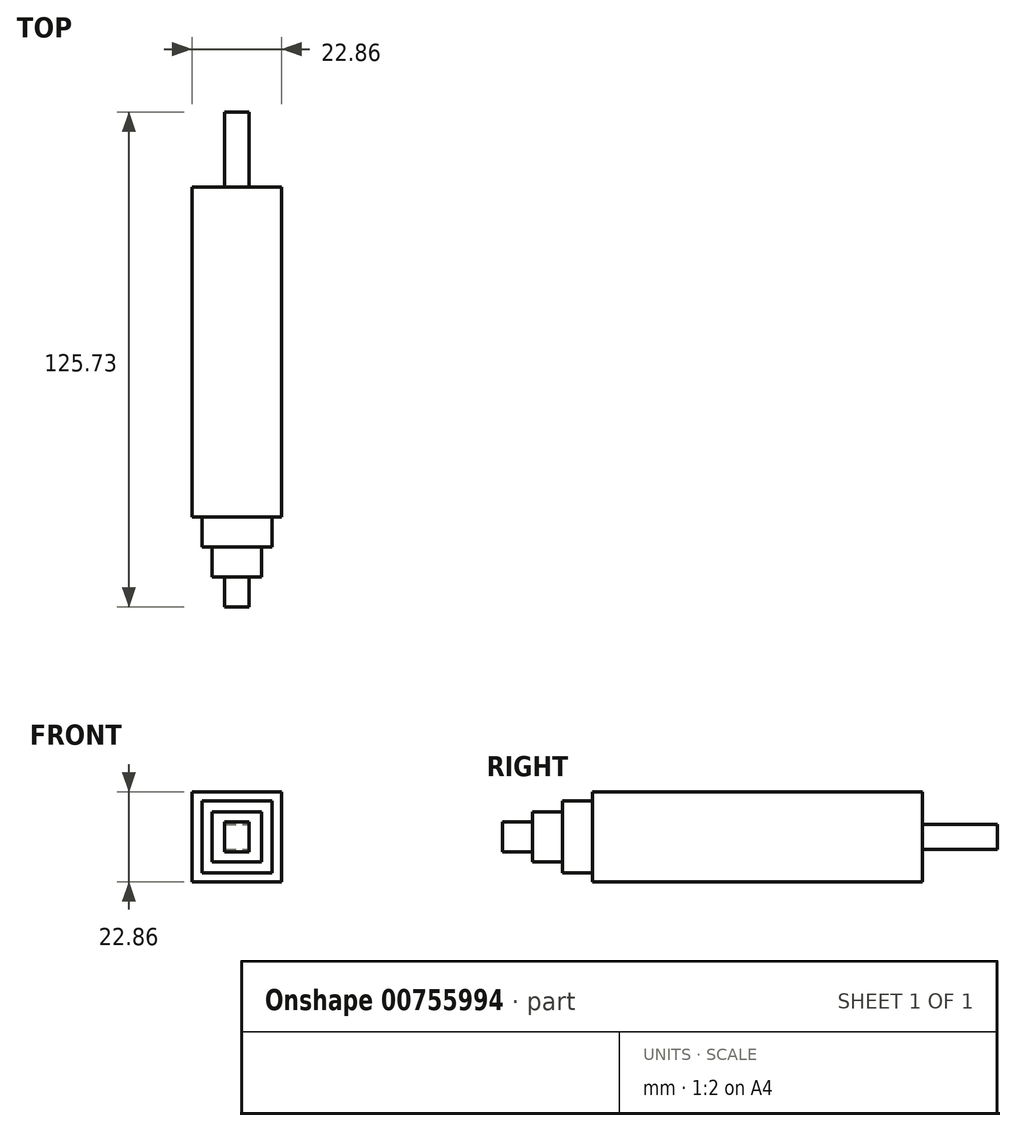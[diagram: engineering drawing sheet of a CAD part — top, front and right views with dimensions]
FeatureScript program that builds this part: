
annotation { "Feature Type Name" : "Feature", "Feature Type Description" : "" }
export const myFeature = defineFeature(function(context is Context, id is Id, definition is map)
    precondition{}
    {
        {
            var Q0;
            Q0=qCreatedBy(makeId("Top.planeOp"),FACE);
            var sketch = newSketch(context, id + "F0", { "sketchPlane" : qUnion([Q0])});
            skLineSegment(sketch, "E0.bottom", {"start": v(0, 0) * mm, "end": v(22.86, 0) * mm});
            skLineSegment(sketch, "E0.top", {"start": v(0, 83.82) * mm, "end": v(22.86, 83.82) * mm});
            skLineSegment(sketch, "E0.left", {"start": v(0, 0) * mm, "end": v(0, 83.82) * mm});
            skLineSegment(sketch, "E0.right", {"start": v(22.86, 0) * mm, "end": v(22.86, 83.82) * mm});
            skSolve(sketch);
        }
        {
            var Q0;
            Q0 = qSketchRegion(id + "F0", true);
            extrude(context, id + "F1", {"entities" : qUnion([Q0]), "depth" : 22.86 * mm, "offsetDistance" : 25.4 * mm});
        }
        {
            var Q0;
            Q0=makeQuery(id+"F1.opExtrude","SWEPT_FACE",FACE,{"disambiguationData":[OSD([sQuery(id+"F0.wireOp",EDGE,"E0.top")])]});
            var sketch = newSketch(context, id + "F2", { "sketchPlane" : qUnion([Q0])});
            skLineSegment(sketch, "E1", {"start": v(-22.86, 11.43) * mm, "end": v(-11.43, 11.43) * mm});
            skLineSegment(sketch, "E2.bottom", {"start": v(-8.25, 14.6) * mm, "end": v(-14.6, 14.6) * mm});
            skLineSegment(sketch, "E2.top", {"start": v(-8.25, 8.26) * mm, "end": v(-14.6, 8.26) * mm});
            skLineSegment(sketch, "E2.left", {"start": v(-8.25, 14.6) * mm, "end": v(-8.25, 8.26) * mm});
            skLineSegment(sketch, "E2.right", {"start": v(-14.6, 14.6) * mm, "end": v(-14.6, 8.26) * mm});
            skPoint(sketch, "E2.middle", {"position": v(-11.43, 11.43) * mm});
            skSolve(sketch);
        }
        {
            var Q0;
            Q0 = qSketchRegion(id + "F2", true);
            extrude(context, id + "F3", {"entities" : qUnion([Q0]), "operationType" : NewBodyOperationType.ADD, "depth" : 19.05 * mm, "offsetDistance" : 25.4 * mm});
        }
        {
            var Q0;
            Q0=makeQuery(id+"F1.opExtrude","SWEPT_FACE",FACE,{"disambiguationData":[OSD([sQuery(id+"F0.wireOp",EDGE,"E0.bottom")])]});
            var sketch = newSketch(context, id + "F4", { "sketchPlane" : qUnion([Q0])});
            skLineSegment(sketch, "E3", {"start": v(0, 11.43) * mm, "end": v(11.43, 11.43) * mm});
            skLineSegment(sketch, "E4.bottom", {"start": v(2.54, 20.56) * mm, "end": v(20.32, 20.56) * mm});
            skLineSegment(sketch, "E4.top", {"start": v(2.54, 2.3) * mm, "end": v(20.32, 2.3) * mm});
            skLineSegment(sketch, "E4.left", {"start": v(2.54, 20.56) * mm, "end": v(2.54, 2.3) * mm});
            skLineSegment(sketch, "E4.right", {"start": v(20.32, 20.56) * mm, "end": v(20.32, 2.3) * mm});
            skPoint(sketch, "E4.middle", {"position": v(11.43, 11.43) * mm});
            skSolve(sketch);
        }
        {
            var Q0;
            Q0 = qSketchRegion(id + "F4", true);
            extrude(context, id + "F5", {"entities" : qUnion([Q0]), "operationType" : NewBodyOperationType.ADD, "depth" : 7.62 * mm, "offsetDistance" : 25.4 * mm});
        }
        {
            var Q0;
            Q0=makeQuery(id+"F5.opExtrude","CAP_FACE",FACE,{"disambiguationData":[OSD([sQuery(id+"F4.wireOp",EDGE,"E4.bottom"),sQuery(id+"F4.wireOp",EDGE,"E4.top"),sQuery(id+"F4.wireOp",EDGE,"E4.left"),sQuery(id+"F4.wireOp",EDGE,"E4.right")])],"isStart":false});
            var sketch = newSketch(context, id + "F6", { "sketchPlane" : qUnion([Q0])});
            skLineSegment(sketch, "E5", {"start": v(2.54, 11.43) * mm, "end": v(15.26, 11.43) * mm});
            skLineSegment(sketch, "E6", {"start": v(11.43, 20.56) * mm, "end": v(11.43, 11.43) * mm});
            skPoint(sketch, "E6.endSnap0", {"position": v(8.9, 11.43) * mm});
            skLineSegment(sketch, "E7.bottom", {"start": v(17.78, 17.78) * mm, "end": v(5.08, 17.78) * mm});
            skLineSegment(sketch, "E7.top", {"start": v(17.78, 5.08) * mm, "end": v(5.08, 5.08) * mm});
            skLineSegment(sketch, "E7.left", {"start": v(17.78, 17.78) * mm, "end": v(17.78, 5.08) * mm});
            skLineSegment(sketch, "E7.right", {"start": v(5.08, 17.78) * mm, "end": v(5.08, 5.08) * mm});
            skPoint(sketch, "E7.middle", {"position": v(11.43, 11.43) * mm});
            skSolve(sketch);
        }
        {
            var Q0;
            Q0 = qSketchRegion(id + "F6", true);
            extrude(context, id + "F7", {"entities" : qUnion([Q0]), "operationType" : NewBodyOperationType.ADD, "depth" : 7.62 * mm, "offsetDistance" : 25.4 * mm});
        }
        {
            var Q0;
            Q0=makeQuery(id+"F7.opExtrude","CAP_FACE",FACE,{"disambiguationData":[OSD([sQuery(id+"F6.wireOp",EDGE,"E7.bottom"),sQuery(id+"F6.wireOp",EDGE,"E7.top"),sQuery(id+"F6.wireOp",EDGE,"E7.left"),sQuery(id+"F6.wireOp",EDGE,"E7.right")])],"isStart":false});
            var sketch = newSketch(context, id + "F8", { "sketchPlane" : qUnion([Q0])});
            skLineSegment(sketch, "E8", {"start": v(5.08, 11.43) * mm, "end": v(11.43, 11.43) * mm});
            skLineSegment(sketch, "E9.bottom", {"start": v(8.26, 15.2) * mm, "end": v(14.6, 15.2) * mm});
            skLineSegment(sketch, "E9.top", {"start": v(8.26, 7.67) * mm, "end": v(14.6, 7.67) * mm});
            skLineSegment(sketch, "E9.left", {"start": v(8.26, 15.2) * mm, "end": v(8.26, 7.67) * mm});
            skLineSegment(sketch, "E9.right", {"start": v(14.6, 15.2) * mm, "end": v(14.6, 7.67) * mm});
            skPoint(sketch, "E9.middle", {"position": v(11.43, 11.43) * mm});
            skPoint(sketch, "E9.cornerSnap0", {"position": v(8.26, 11.43) * mm});
            skSolve(sketch);
        }
        {
            var Q0;
            Q0 = qSketchRegion(id + "F8", true);
            extrude(context, id + "F9", {"entities" : qUnion([Q0]), "operationType" : NewBodyOperationType.ADD, "depth" : 7.62 * mm, "offsetDistance" : 25.4 * mm});
        }
    });
